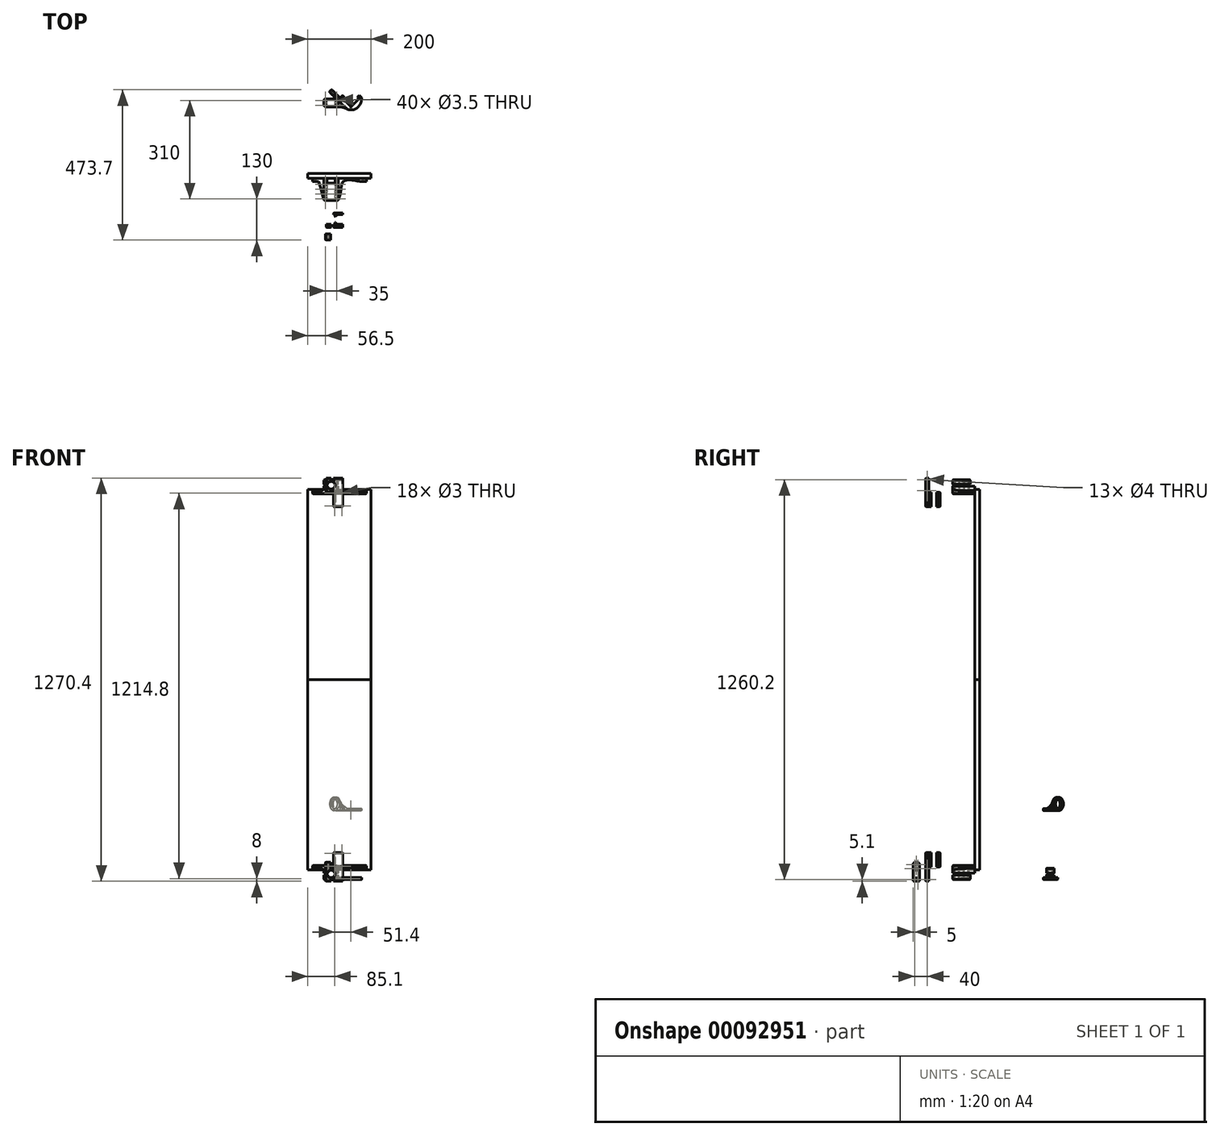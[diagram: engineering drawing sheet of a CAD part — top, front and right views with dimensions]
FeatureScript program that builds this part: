
annotation { "Feature Type Name" : "Feature", "Feature Type Description" : "" }
export const myFeature = defineFeature(function(context is Context, id is Id, definition is map)
    precondition{}
    {
        {
            var Q0;
            Q0=qCreatedBy(makeId("Top.planeOp"),FACE);
            var sketch = newSketch(context, id + "F0", { "sketchPlane" : qUnion([Q0])});
            skLineSegment(sketch, "E0", {"start": v(-59, 0) * mm, "end": v(111, 0) * mm});
            skLineSegment(sketch, "E1", {"start": v(-59, 0) * mm, "end": v(-59, -10) * mm});
            skLineSegment(sketch, "E2", {"start": v(-59, -10) * mm, "end": v(-39, -10) * mm});
            skLineSegment(sketch, "E3", {"start": v(-39, -10) * mm, "end": v(-22.5, -70) * mm});
            skLineSegment(sketch, "E4", {"start": v(-22.5, -70) * mm, "end": v(22.5, -70) * mm});
            skLineSegment(sketch, "E5", {"start": v(22.5, -70) * mm, "end": v(39, -10) * mm});
            skLineSegment(sketch, "E6", {"start": v(39, -10) * mm, "end": v(111, -10) * mm});
            skLineSegment(sketch, "E7", {"start": v(111, -10) * mm, "end": v(111, 0) * mm});
            skLineSegment(sketch, "E8", {"start": v(-49, 0) * mm, "end": v(-49, -10) * mm});
            skLineSegment(sketch, "E9", {"start": v(101, 0) * mm, "end": v(101, -10) * mm});
            skLineSegment(sketch, "E10.bottom", {"start": v(-59, 15) * mm, "end": v(141, 15) * mm, "construction": true});
            skLineSegment(sketch, "E10.top", {"start": v(-59, 0) * mm, "end": v(141, 0) * mm, "construction": true});
            skLineSegment(sketch, "E10.left", {"start": v(-59, 15) * mm, "end": v(-59, 0) * mm, "construction": true});
            skLineSegment(sketch, "E10.right", {"start": v(141, 15) * mm, "end": v(141, 0) * mm, "construction": true});
            skLineSegment(sketch, "E11", {"start": v(12.6, -70) * mm, "end": v(12.6, 0) * mm, "construction": true});
            skLineSegment(sketch, "E12", {"start": v(-12.6, -70) * mm, "end": v(-12.6, 0) * mm, "construction": true});
            skLineSegment(sketch, "E13", {"start": v(-12.6, -70) * mm, "end": v(12.6, -70) * mm});
            skPoint(sketch, "E14", {"position": v(0, -70) * mm});
            skFitSpline(sketch, "E15", {"points": [v(22.5, -70) * mm, v(91, -10) * mm], "startDerivative": vector(24.75, 90) * mm, "endDerivative": vector(156, 0) * mm});
            skLineSegment(sketch, "E16", {"start": v(0, 0) * mm, "end": v(0, -70) * mm});
            skSolve(sketch);
        }
        {
            var Q0;
            Q0=qCreatedBy(makeId("Top.planeOp"),FACE);
            cPlane(context, id + "F1", {"entities" : qUnion([Q0]), "cplaneType" : CPlaneType.OFFSET, "offset" : 3 * mm, "width" : 150 * mm, "height" : 150 * mm});
        }
        {
            var Q0;
            Q0=qCreatedBy(id+"F1.planeOp",FACE);
            var sketch = newSketch(context, id + "F2", { "sketchPlane" : qUnion([Q0])});
            skLineSegment(sketch, "E17.bottom", {"start": v(17.5, -65) * mm, "end": v(-17.5, -65) * mm, "construction": true});
            skLineSegment(sketch, "E17.top", {"start": v(17.5, -20) * mm, "end": v(-17.5, -20) * mm, "construction": true});
            skLineSegment(sketch, "E17.left", {"start": v(17.5, -65) * mm, "end": v(17.5, -20) * mm, "construction": true});
            skLineSegment(sketch, "E17.right", {"start": v(-17.5, -65) * mm, "end": v(-17.5, -20) * mm, "construction": true});
            skPoint(sketch, "E17.middle", {"position": v(0, -42.5) * mm});
            skLineSegment(sketch, "E18.bottom", {"start": v(17.5, -50) * mm, "end": v(-17.5, -50) * mm, "construction": true});
            skLineSegment(sketch, "E18.top", {"start": v(17.5, -35) * mm, "end": v(-17.5, -35) * mm, "construction": true});
            skLineSegment(sketch, "E18.left", {"start": v(17.5, -50) * mm, "end": v(17.5, -35) * mm, "construction": true});
            skLineSegment(sketch, "E18.right", {"start": v(-17.5, -50) * mm, "end": v(-17.5, -35) * mm, "construction": true});
            skCircle(sketch, "E19", {"center": v(-17.5, -20) * mm, "radius": 1.75 * mm});
            skCircle(sketch, "E20", {"center": v(-17.5, -35) * mm, "radius": 1.75 * mm});
            skCircle(sketch, "E21", {"center": v(-17.5, -50) * mm, "radius": 1.75 * mm});
            skCircle(sketch, "E22", {"center": v(-17.5, -65) * mm, "radius": 1.75 * mm});
            skCircle(sketch, "E23", {"center": v(17.5, -20) * mm, "radius": 1.75 * mm});
            skCircle(sketch, "E24", {"center": v(17.5, -35) * mm, "radius": 1.75 * mm});
            skCircle(sketch, "E25", {"center": v(17.5, -50) * mm, "radius": 1.75 * mm});
            skCircle(sketch, "E26", {"center": v(17.5, -65) * mm, "radius": 1.75 * mm});
            skSolve(sketch);
        }
        {
            var Q0;
            Q0=qCreatedBy(makeId("Front.planeOp"),FACE);
            var sketch = newSketch(context, id + "F3", { "sketchPlane" : qUnion([Q0])});
            skCircle(sketch, "E27", {"center": v(0, 0) * mm, "radius": 12.6 * mm});
            skLineSegment(sketch, "E28.bottom", {"start": v(-22.5, 3) * mm, "end": v(22.5, 3) * mm});
            skLineSegment(sketch, "E28.top", {"start": v(-22.5, 27.6) * mm, "end": v(22.5, 27.6) * mm});
            skLineSegment(sketch, "E28.left", {"start": v(-22.5, 3) * mm, "end": v(-22.5, 27.6) * mm});
            skLineSegment(sketch, "E28.right", {"start": v(22.5, 3) * mm, "end": v(22.5, 27.6) * mm});
            skPoint(sketch, "E29", {"position": v(0, 12.6) * mm});
            skPoint(sketch, "E30", {"position": v(0, 27.6) * mm});
            skLineSegment(sketch, "E31.bottom", {"start": v(-22.5, -3) * mm, "end": v(22.5, -3) * mm});
            skLineSegment(sketch, "E31.top", {"start": v(-22.5, -17.6) * mm, "end": v(22.5, -17.6) * mm});
            skLineSegment(sketch, "E31.left", {"start": v(-22.5, -3) * mm, "end": v(-22.5, -17.6) * mm});
            skLineSegment(sketch, "E31.right", {"start": v(22.5, -3) * mm, "end": v(22.5, -17.6) * mm});
            skLineSegment(sketch, "E32", {"start": v(0, 3) * mm, "end": v(0, 0) * mm, "construction": true});
            skLineSegment(sketch, "E33", {"start": v(0, 0) * mm, "end": v(0, -3) * mm, "construction": true});
            skPoint(sketch, "E34", {"position": v(0, -12.6) * mm});
            skPoint(sketch, "E35", {"position": v(0, -17.6) * mm});
            skSolve(sketch);
        }
        {
            var Q0;
            Q0=makeQuery(id+"F3.imprint","IMPRINT",FACE,{"disambiguationData":[TD([[makeQuery(id+"F3.imprint","IMPRINT",EDGE,{"derivedFrom":sQuery(id+"F3.wireOp",EDGE,"E28.top")}),-1.0]])]});
            extrude(context, id + "F4", {"entities" : qUnion([Q0]), "depth" : 70 * mm});
        }
        {
            var Q0;
            Q0=makeQuery(id+"F4.opExtrude","SWEPT_FACE",FACE,{"disambiguationData":[OSD([sQuery(id+"F3.wireOp",EDGE,"E28.top")])]});
            var sketch = newSketch(context, id + "F5", { "sketchPlane" : qUnion([Q0])});
            skLineSegment(sketch, "E36.0", {"start": v(-59, 0) * mm, "end": v(-59, -10) * mm});
            skLineSegment(sketch, "E36.1", {"start": v(-59, 0) * mm, "end": v(111, 0) * mm});
            skLineSegment(sketch, "E36.2", {"start": v(111, -10) * mm, "end": v(111, 0) * mm});
            skLineSegment(sketch, "E36.3", {"start": v(91, -10) * mm, "end": v(111, -10) * mm});
            skFitSpline(sketch, "E36.4", {"points": [v(22.5, -70) * mm, v(30.75, -40) * mm, v(39, -10) * mm, v(91, -10) * mm]});
            skLineSegment(sketch, "E36.5", {"start": v(-22.5, -70) * mm, "end": v(22.5, -70) * mm});
            skLineSegment(sketch, "E36.6", {"start": v(-39, -10) * mm, "end": v(-22.5, -70) * mm});
            skLineSegment(sketch, "E36.7", {"start": v(-59, -10) * mm, "end": v(-39, -10) * mm});
            skPoint(sketch, "E37.orphan", {"position": v(39, -10) * mm});
            skSolve(sketch);
        }
        {
            var Q0;
            Q0 = qSketchRegion(id + "F5", true);
            extrude(context, id + "F6", {"entities" : qUnion([Q0]), "operationType" : NewBodyOperationType.ADD, "oppositeDirection" : true, "depth" : 10 * mm});
        }
        {
            var Q0;
            Q0=makeQuery(id+"F4.opExtrude","CAP_FACE",FACE,{"disambiguationData":[OSD([sQuery(id+"F3.wireOp",EDGE,"E27"),sQuery(id+"F3.wireOp",EDGE,"E28.bottom"),sQuery(id+"F3.wireOp",EDGE,"E28.top"),sQuery(id+"F3.wireOp",EDGE,"E28.left"),sQuery(id+"F3.wireOp",EDGE,"E28.right")])],"isStart":false});
            var sketch = newSketch(context, id + "F7", { "sketchPlane" : qUnion([Q0])});
            skLineSegment(sketch, "E38.0", {"start": v(-22.5, -3) * mm, "end": v(-22.5, -17.6) * mm});
            skLineSegment(sketch, "E38.1", {"start": v(-22.5, -3) * mm, "end": v(-12.24, -3) * mm});
            skArc(sketch, "E38.2", {"start": v(-12.24, -3) * mm, "mid": v(0, -12.6) * mm, "end": v(12.24, -3) * mm});
            skLineSegment(sketch, "E38.3", {"start": v(22.5, -3) * mm, "end": v(22.5, -17.6) * mm});
            skLineSegment(sketch, "E38.4", {"start": v(-22.5, -17.6) * mm, "end": v(22.5, -17.6) * mm});
            skLineSegment(sketch, "E39.trimOffspring", {"start": v(12.24, -3) * mm, "end": v(22.5, -3) * mm});
            skSolve(sketch);
        }
        {
            var Q0;
            Q0 = qSketchRegion(id + "F7", true);
            extrude(context, id + "F8", {"entities" : qUnion([Q0]), "oppositeDirection" : true, "depth" : 55 * mm});
        }
        {
            var Q0;
            Q0=makeQuery(id+"F6.boolean.opBoolean","INTERSECT",EDGE,{"derivedFrom":[makeQuery(id+"F4.opExtrude","SWEPT_FACE",FACE,{"disambiguationData":[OSD([sQuery(id+"F3.wireOp",EDGE,"E28.left")])]}),makeQuery(id+"F6.opExtrude","CAP_FACE",FACE,{"disambiguationData":[OSD([sQuery(id+"F5.wireOp",EDGE,"E36.0"),sQuery(id+"F5.wireOp",EDGE,"E36.1"),sQuery(id+"F5.wireOp",EDGE,"E36.2"),sQuery(id+"F5.wireOp",EDGE,"E36.3"),sQuery(id+"F5.wireOp",EDGE,"E36.4"),sQuery(id+"F5.wireOp",EDGE,"E36.5"),sQuery(id+"F5.wireOp",EDGE,"E36.6"),sQuery(id+"F5.wireOp",EDGE,"E36.7")])],"isStart":false})]});
            var Q1;
            Q1=makeQuery(id+"F6.boolean.opBoolean","INTERSECT",EDGE,{"derivedFrom":[makeQuery(id+"F4.opExtrude","SWEPT_FACE",FACE,{"disambiguationData":[OSD([sQuery(id+"F3.wireOp",EDGE,"E28.right")])]}),makeQuery(id+"F6.opExtrude","CAP_FACE",FACE,{"disambiguationData":[OSD([sQuery(id+"F5.wireOp",EDGE,"E36.0"),sQuery(id+"F5.wireOp",EDGE,"E36.1"),sQuery(id+"F5.wireOp",EDGE,"E36.2"),sQuery(id+"F5.wireOp",EDGE,"E36.3"),sQuery(id+"F5.wireOp",EDGE,"E36.4"),sQuery(id+"F5.wireOp",EDGE,"E36.5"),sQuery(id+"F5.wireOp",EDGE,"E36.6"),sQuery(id+"F5.wireOp",EDGE,"E36.7")])],"isStart":false})]});
            fillet(context, id + "F9", {"entities" : qUnion([Q0, Q1]), "radius" : 10 * mm, "tangentPropagation" : true, "allowEdgeOverflow" : false});
        }
        {
            var Q0;
            {var subQ0=sQuery(id+"F3.wireOp",EDGE,"E28.left");Q0=makeQuery(id+"F6.boolean.opBoolean","MERGE",EDGE,{"derivedFrom":[makeQuery(id+"F4.opExtrude","CAP_EDGE",EDGE,{"disambiguationData":[OSD([subQ0])],"isStart":false}),makeQuery(id+"F6.opExtrude","SWEPT_EDGE",EDGE,{"disambiguationData":[OSD([sQuery(id+"F3.wireOp",EDGE,"E28.top"),subQ0,sQuery(id+"F5.wireOp",EDGE,"E36.5"),sQuery(id+"F5.wireOp",EDGE,"E36.6")])]})]});}
            var Q1;
            {var subQ0=sQuery(id+"F3.wireOp",EDGE,"E28.right");Q1=makeQuery(id+"F6.boolean.opBoolean","MERGE",EDGE,{"derivedFrom":[makeQuery(id+"F4.opExtrude","CAP_EDGE",EDGE,{"disambiguationData":[OSD([subQ0])],"isStart":false}),makeQuery(id+"F6.opExtrude","SWEPT_EDGE",EDGE,{"disambiguationData":[OSD([sQuery(id+"F3.wireOp",EDGE,"E28.top"),subQ0,sQuery(id+"F5.wireOp",EDGE,"E36.4"),sQuery(id+"F5.wireOp",EDGE,"E36.5")])]})]});}
            var Q2;
            Q2=makeQuery(id+"F8.opExtrude","CAP_EDGE",EDGE,{"disambiguationData":[OSD([sQuery(id+"F7.wireOp",EDGE,"E38.3")])],"isStart":true});
            var Q3;
            Q3=makeQuery(id+"F8.opExtrude","CAP_EDGE",EDGE,{"disambiguationData":[OSD([sQuery(id+"F7.wireOp",EDGE,"E38.0")])],"isStart":true});
            var Q4;
            Q4=makeQuery(id+"F8.opExtrude","CAP_EDGE",EDGE,{"disambiguationData":[OSD([sQuery(id+"F7.wireOp",EDGE,"E38.0")])],"isStart":false});
            var Q5;
            Q5=makeQuery(id+"F8.opExtrude","CAP_EDGE",EDGE,{"disambiguationData":[OSD([sQuery(id+"F7.wireOp",EDGE,"E38.3")])],"isStart":false});
            fillet(context, id + "F10", {"entities" : qUnion([Q0, Q1, Q2, Q3, Q4, Q5]), "radius" : 5 * mm, "tangentPropagation" : true, "allowEdgeOverflow" : false});
        }
        {
            var Q0;
            Q0 = qSketchRegion(id + "F2", true);
            extrude(context, id + "F11", {"entities" : qUnion([Q0]), "operationType" : NewBodyOperationType.REMOVE, "endBound" : BoundingType.SYMMETRIC, "oppositeDirection" : true, "depth" : 50 * mm});
        }
        {
            var Q0;
            Q0=makeQuery(id+"F8.opExtrude","SWEPT_EDGE",EDGE,{"disambiguationData":[OSD([sQuery(id+"F7.wireOp",EDGE,"E38.0"),sQuery(id+"F7.wireOp",EDGE,"E38.4")])]});
            var Q1;
            Q1=makeQuery(id+"F6.boolean.opBoolean","MERGE",EDGE,{"derivedFrom":[makeQuery(id+"F4.opExtrude","CAP_EDGE",EDGE,{"disambiguationData":[OSD([sQuery(id+"F3.wireOp",EDGE,"E28.top")])],"isStart":true}),makeQuery(id+"F6.opExtrude","CAP_EDGE",EDGE,{"disambiguationData":[OSD([sQuery(id+"F5.wireOp",EDGE,"E36.1")])],"isStart":true})]});
            var Q2;
            Q2=makeQuery(id+"F6.opExtrude","CAP_EDGE",EDGE,{"disambiguationData":[OSD([sQuery(id+"F5.wireOp",EDGE,"E36.6")])],"isStart":true});
            var Q3;
            Q3=makeQuery(id+"F6.opExtrude","CAP_EDGE",EDGE,{"disambiguationData":[OSD([sQuery(id+"F5.wireOp",EDGE,"E36.0")])],"isStart":true});
            var Q4;
            Q4=makeQuery(id+"F6.opExtrude","CAP_EDGE",EDGE,{"disambiguationData":[OSD([sQuery(id+"F5.wireOp",EDGE,"E36.2")])],"isStart":true});
            chamfer(context, id + "F12", {"entities" : qUnion([Q0, Q1, Q2, Q3, Q4]), "width" : 2 * mm, "tangentPropagation" : true});
        }
        {
            var Q0;
            Q0=makeQuery(id+"F6.boolean.opBoolean","MERGE",FACE,{"derivedFrom":[makeQuery(id+"F4.opExtrude","CAP_FACE",FACE,{"disambiguationData":[OSD([sQuery(id+"F3.wireOp",EDGE,"E27"),sQuery(id+"F3.wireOp",EDGE,"E28.bottom"),sQuery(id+"F3.wireOp",EDGE,"E28.top"),sQuery(id+"F3.wireOp",EDGE,"E28.left"),sQuery(id+"F3.wireOp",EDGE,"E28.right")])],"isStart":true}),makeQuery(id+"F6.opExtrude","SWEPT_FACE",FACE,{"disambiguationData":[OSD([sQuery(id+"F5.wireOp",EDGE,"E36.1")])]})]});
            var sketch = newSketch(context, id + "F13", { "sketchPlane" : qUnion([Q0])});
            skCircle(sketch, "E40", {"center": v(-101, 22.6) * mm, "radius": 2 * mm});
            skCircle(sketch, "E41", {"center": v(49, 22.6) * mm, "radius": 2 * mm});
            skSolve(sketch);
        }
        {
            var Q0;
            Q0 = qSketchRegion(id + "F13", true);
            var Q1;
            Q1=makeQuery(id+"F6.opExtrude","SWEPT_FACE",FACE,{"disambiguationData":[OSD([sQuery(id+"F5.wireOp",EDGE,"E36.3")])]});
            extrude(context, id + "F14", {"entities" : qUnion([Q0]), "operationType" : NewBodyOperationType.REMOVE, "endBound" : BoundingType.UP_TO_SURFACE, "oppositeDirection" : true, "endBoundEntityFace" : qUnion([Q1]), "depth" : 25 * mm});
        }
        {
            var Q0;
            Q0=qCreatedBy(makeId("Right.planeOp"),FACE);
            var sketch = newSketch(context, id + "F15", { "sketchPlane" : qUnion([Q0])});
            skLineSegment(sketch, "E42", {"start": v(-70, 12.6) * mm, "end": v(-69.5, 11.73) * mm});
            skLineSegment(sketch, "E43", {"start": v(-69.5, 11.73) * mm, "end": v(-69, 12.6) * mm});
            skLineSegment(sketch, "E44", {"start": v(-69, 12.6) * mm, "end": v(-70, 12.6) * mm});
            skSolve(sketch);
        }
        {
            var Q0;
            Q0 = qSketchRegion(id + "F15", true);
            var Q1;
            Q1=sQuery(id+"F0.wireOp",EDGE,"E16");
            revolve(context, id + "F16", {"operationType" : NewBodyOperationType.ADD, "entities" : qUnion([Q0]), "axis" : qUnion([Q1]), "revolveType" : RevolveType.FULL});
        }
        {
            var Q0;
            Q0=makeQuery(id+"F4.opExtrude","CAP_FACE",FACE,{"disambiguationData":[OSD([sQuery(id+"F3.wireOp",EDGE,"E27"),sQuery(id+"F3.wireOp",EDGE,"E28.bottom"),sQuery(id+"F3.wireOp",EDGE,"E28.top"),sQuery(id+"F3.wireOp",EDGE,"E28.left"),sQuery(id+"F3.wireOp",EDGE,"E28.right")])],"isStart":false});
            var sketch = newSketch(context, id + "F17", { "sketchPlane" : qUnion([Q0])});
            skLineSegment(sketch, "E45.bottom", {"start": v(-17.5, -3) * mm, "end": v(18.7, -3) * mm});
            skLineSegment(sketch, "E45.top", {"start": v(-17.5, 3) * mm, "end": v(18.7, 3) * mm});
            skLineSegment(sketch, "E45.left", {"start": v(-17.5, -3) * mm, "end": v(-17.5, 3) * mm});
            skLineSegment(sketch, "E45.right", {"start": v(18.7, -3) * mm, "end": v(18.7, 3) * mm});
            skSolve(sketch);
        }
        {
            var Q0;
            Q0 = qSketchRegion(id + "F17", true);
            extrude(context, id + "F18", {"entities" : qUnion([Q0]), "operationType" : NewBodyOperationType.REMOVE, "oppositeDirection" : true, "depth" : 25 * mm});
        }
        {
            var Q0;
            Q0=qCreatedBy(makeId("Front.planeOp"),FACE);
            var sketch = newSketch(context, id + "F19", { "sketchPlane" : qUnion([Q0])});
            skLineSegment(sketch, "E46.bottom", {"start": v(-74, 612.6) * mm, "end": v(126, 612.6) * mm});
            skLineSegment(sketch, "E46.top", {"start": v(-74, 12.6) * mm, "end": v(126, 12.6) * mm});
            skLineSegment(sketch, "E46.left", {"start": v(-74, 612.6) * mm, "end": v(-74, 12.6) * mm});
            skLineSegment(sketch, "E46.right", {"start": v(126, 612.6) * mm, "end": v(126, 12.6) * mm});
            skLineSegment(sketch, "E47.bottom", {"start": v(126, 12.6) * mm, "end": v(101, 12.6) * mm, "construction": true});
            skLineSegment(sketch, "E47.top", {"start": v(126, 22.6) * mm, "end": v(101, 22.6) * mm, "construction": true});
            skLineSegment(sketch, "E47.left", {"start": v(126, 12.6) * mm, "end": v(126, 22.6) * mm, "construction": true});
            skLineSegment(sketch, "E47.right", {"start": v(101, 12.6) * mm, "end": v(101, 22.6) * mm, "construction": true});
            skLineSegment(sketch, "E48", {"start": v(101, 22.6) * mm, "end": v(-49, 22.6) * mm, "construction": true});
            skSolve(sketch);
        }
        {
            var Q0;
            Q0=makeQuery(id+"F19.imprint","IMPRINT",FACE,{"disambiguationData":[TD([[makeQuery(id+"F19.imprint","IMPRINT",EDGE,{"derivedFrom":sQuery(id+"F19.wireOp",EDGE,"E46.bottom")}),-1.0]])]});
            extrude(context, id + "F20", {"entities" : qUnion([Q0]), "oppositeDirection" : true, "depth" : 15 * mm});
        }
        {
            var Q0;
            Q0=qCreatedBy(makeId("Front.planeOp"),FACE);
            cPlane(context, id + "F21", {"entities" : qUnion([Q0]), "cplaneType" : CPlaneType.OFFSET, "offset" : 150 * mm, "width" : 150 * mm, "height" : 150 * mm});
        }
        {
            var Q0;
            Q0=qCreatedBy(id+"F21.planeOp",FACE);
            var sketch = newSketch(context, id + "F22", { "sketchPlane" : qUnion([Q0])});
            skCircle(sketch, "E49.0", {"center": v(0, 0) * mm, "radius": 12.6 * mm});
            skLineSegment(sketch, "E50.bottom", {"start": v(8.1, -22.6) * mm, "end": v(37.1, -22.6) * mm});
            skLineSegment(sketch, "E50.top", {"start": v(8.1, 68) * mm, "end": v(37.1, 68) * mm});
            skLineSegment(sketch, "E50.left", {"start": v(8.1, -22.6) * mm, "end": v(8.1, 68) * mm});
            skLineSegment(sketch, "E50.right", {"start": v(37.1, -22.6) * mm, "end": v(37.1, 68) * mm});
            skPoint(sketch, "E51", {"position": v(12.6, 0) * mm});
            skLineSegment(sketch, "E52", {"start": v(12.6, 68) * mm, "end": v(12.6, -22.6) * mm, "construction": true});
            skLineSegment(sketch, "E53", {"start": v(32.6, 68) * mm, "end": v(32.6, -22.6) * mm, "construction": true});
            skLineSegment(sketch, "E54.bottom", {"start": v(11.1, 25) * mm, "end": v(34.1, 25) * mm, "construction": true});
            skLineSegment(sketch, "E54.top", {"start": v(11.1, 65) * mm, "end": v(34.1, 65) * mm, "construction": true});
            skLineSegment(sketch, "E54.left", {"start": v(11.1, 25) * mm, "end": v(11.1, 65) * mm, "construction": true});
            skLineSegment(sketch, "E54.right", {"start": v(34.1, 25) * mm, "end": v(34.1, 65) * mm, "construction": true});
            skCircle(sketch, "E55", {"center": v(11.1, 65) * mm, "radius": 1.5 * mm});
            skCircle(sketch, "E56", {"center": v(11.1, 25) * mm, "radius": 1.5 * mm});
            skCircle(sketch, "E57", {"center": v(34.1, 25) * mm, "radius": 1.5 * mm});
            skCircle(sketch, "E58", {"center": v(34.1, 65) * mm, "radius": 1.5 * mm});
            skPoint(sketch, "E59", {"position": v(22.6, 68) * mm});
            skPoint(sketch, "E60", {"position": v(22.6, 65) * mm});
            skLineSegment(sketch, "E61", {"start": v(12.6, 17.5) * mm, "end": v(12.6, -17.5) * mm, "construction": true});
            skLineSegment(sketch, "E62.bottom", {"start": v(-15.6, -22.6) * mm, "end": v(0, -22.6) * mm});
            skLineSegment(sketch, "E62.top", {"start": v(-15.6, 22.6) * mm, "end": v(0, 22.6) * mm});
            skLineSegment(sketch, "E62.left", {"start": v(-15.6, -22.6) * mm, "end": v(-15.6, 22.6) * mm});
            skLineSegment(sketch, "E62.right", {"start": v(0, -22.6) * mm, "end": v(0, 22.6) * mm});
            skPoint(sketch, "E63", {"position": v(-12.6, 0) * mm});
            skSolve(sketch);
        }
        {
            var Q0;
            {var subQ1=sQuery(id+"F22.wireOp",EDGE,"E50.bottom");Q0=makeQuery(id+"F22.imprint","IMPRINT",FACE,{"disambiguationData":[TD([[makeQuery(id+"F22.imprint","IMPRINT",EDGE,{"derivedFrom":subQ1}),1.0]])]});}
            var Q1;
            {var subQ4=sQuery(id+"F22.wireOp",EDGE,"E62.bottom");Q1=makeQuery(id+"F22.imprint","IMPRINT",FACE,{"disambiguationData":[TD([[makeQuery(id+"F22.imprint","IMPRINT",EDGE,{"derivedFrom":subQ4}),1.0]])]});}
            extrude(context, id + "F23", {"entities" : qUnion([Q0, Q1]), "endBound" : BoundingType.SYMMETRIC, "depth" : 10 * mm});
        }
        {
            var Q0;
            Q0=makeQuery(id+"F23.opExtrude","SWEPT_FACE",FACE,{"disambiguationData":[OSD([sQuery(id+"F22.wireOp",EDGE,"E50.top")])]});
            var sketch = newSketch(context, id + "F24", { "sketchPlane" : qUnion([Q0])});
            skLineSegment(sketch, "E64", {"start": v(8.1, -155) * mm, "end": v(8.1, -135) * mm, "construction": true});
            skPoint(sketch, "E64.endSnap0", {"position": v(8.1, -150) * mm});
            skLineSegment(sketch, "E65", {"start": v(8.1, -135) * mm, "end": v(14.1, -135) * mm, "construction": true});
            skLineSegment(sketch, "E66", {"start": v(14.1, -135) * mm, "end": v(14.1, -145) * mm, "construction": true});
            skLineSegment(sketch, "E67", {"start": v(14.1, -145) * mm, "end": v(37.1, -145) * mm, "construction": true});
            skLineSegment(sketch, "E68", {"start": v(37.1, -145) * mm, "end": v(37.1, -155) * mm});
            skLineSegment(sketch, "E69", {"start": v(37.1, -155) * mm, "end": v(8.1, -155) * mm});
            skLineSegment(sketch, "E70", {"start": v(8.1, -125) * mm, "end": v(8.1, -110) * mm, "construction": true});
            skLineSegment(sketch, "E71", {"start": v(8.1, -110) * mm, "end": v(37.1, -110) * mm});
            skLineSegment(sketch, "E72", {"start": v(37.1, -110) * mm, "end": v(37.1, -115) * mm});
            skLineSegment(sketch, "E73", {"start": v(37.1, -115) * mm, "end": v(14.1, -115) * mm, "construction": true});
            skLineSegment(sketch, "E74", {"start": v(14.1, -115) * mm, "end": v(14.1, -125) * mm, "construction": true});
            skLineSegment(sketch, "E75", {"start": v(14.1, -125) * mm, "end": v(8.1, -125) * mm, "construction": true});
            skLineSegment(sketch, "E76", {"start": v(12.6, -145) * mm, "end": v(12.6, -135) * mm});
            skArc(sketch, "E77", {"start": v(12.6, -135) * mm, "mid": v(15.53, -142.07) * mm, "end": v(22.6, -145) * mm});
            skLineSegment(sketch, "E78", {"start": v(22.6, -145) * mm, "end": v(37.1, -145) * mm});
            skLineSegment(sketch, "E79", {"start": v(8.1, -150) * mm, "end": v(8.1, -145) * mm});
            skLineSegment(sketch, "E80", {"start": v(8.1, -145) * mm, "end": v(12.6, -145) * mm});
            skArc(sketch, "E81", {"start": v(22.6, -115) * mm, "mid": v(15.53, -117.93) * mm, "end": v(12.6, -125) * mm});
            skLineSegment(sketch, "E82", {"start": v(8.1, -110) * mm, "end": v(8.1, -115) * mm});
            skLineSegment(sketch, "E83", {"start": v(8.1, -115) * mm, "end": v(12.6, -115) * mm});
            skLineSegment(sketch, "E84", {"start": v(12.6, -115) * mm, "end": v(12.6, -125) * mm});
            skLineSegment(sketch, "E85", {"start": v(22.6, -115) * mm, "end": v(37.1, -115) * mm});
            skSolve(sketch);
        }
        {
            var Q0;
            Q0=makeQuery(id+"F24.imprint","IMPRINT",FACE,{"disambiguationData":[TD([[makeQuery(id+"F24.imprint","IMPRINT",EDGE,{"derivedFrom":sQuery(id+"F24.wireOp",EDGE,"E71")}),-1.0]])]});
            var Q1;
            {var subQ0=sQuery(id+"F24.wireOp",EDGE,"E76");Q1=makeQuery(id+"F24.imprint","IMPRINT",FACE,{"disambiguationData":[TD([[makeQuery(id+"F24.imprint","IMPRINT",EDGE,{"derivedFrom":subQ0}),-1.0]])]});}
            extrude(context, id + "F25", {"entities" : qUnion([Q0, Q1]), "operationType" : NewBodyOperationType.ADD, "oppositeDirection" : true, "depth" : 46 * mm});
        }
        {
            var Q0;
            Q0=makeQuery(id+"F25.opExtrude","SWEPT_FACE",FACE,{"disambiguationData":[OSD([sQuery(id+"F24.wireOp",EDGE,"E71")])]});
            var sketch = newSketch(context, id + "F26", { "sketchPlane" : qUnion([Q0])});
            skCircle(sketch, "E86.0", {"center": v(-11.1, 25) * mm, "radius": 1.5 * mm});
            skCircle(sketch, "E86.1", {"center": v(-11.1, 65) * mm, "radius": 1.5 * mm});
            skCircle(sketch, "E86.2", {"center": v(-34.1, 25) * mm, "radius": 1.5 * mm});
            skCircle(sketch, "E86.3", {"center": v(-34.1, 65) * mm, "radius": 1.5 * mm});
            skSolve(sketch);
        }
        {
            var Q0;
            Q0 = qSketchRegion(id + "F26", true);
            extrude(context, id + "F27", {"entities" : qUnion([Q0]), "operationType" : NewBodyOperationType.REMOVE, "oppositeDirection" : true, "depth" : 25 * mm});
        }
        {
            var Q0;
            Q0=makeQuery(id+"F23.opExtrude","SWEPT_FACE",FACE,{"disambiguationData":[OSD([sQuery(id+"F22.wireOp",EDGE,"E50.right")])]});
            var sketch = newSketch(context, id + "F28", { "sketchPlane" : qUnion([Q0])});
            skPoint(sketch, "E87.0", {"position": v(-150, 17.5) * mm});
            skPoint(sketch, "E87.1", {"position": v(-150, -17.5) * mm});
            skCircle(sketch, "E88", {"center": v(-150, 17.5) * mm, "radius": 2 * mm});
            skCircle(sketch, "E89", {"center": v(-150, -17.5) * mm, "radius": 2 * mm});
            skSolve(sketch);
        }
        {
            var Q0;
            Q0 = qSketchRegion(id + "F28", true);
            extrude(context, id + "F29", {"entities" : qUnion([Q0]), "operationType" : NewBodyOperationType.REMOVE, "oppositeDirection" : true, "depth" : 55 * mm});
        }
        {
            var Q0;
            Q0=makeQuery(id+"F23.opExtrude","CAP_EDGE",EDGE,{"disambiguationData":[OSD([sQuery(id+"F22.wireOp",EDGE,"E50.right")])],"isStart":false});
            var Q1;
            Q1=makeQuery(id+"F23.opExtrude","CAP_EDGE",EDGE,{"disambiguationData":[OSD([sQuery(id+"F22.wireOp",EDGE,"E50.bottom")])],"isStart":false});
            var Q2;
            {var subQ0=sQuery(id+"F22.wireOp",EDGE,"E50.left");Q2=makeQuery(id+"F23.opExtrude","CAP_EDGE",EDGE,{"disambiguationData":[OSD([subQ0]),TDD([makeQuery(id+"F22.imprint","IMPRINT",EDGE,{"disambiguationData":[TD([[makeQuery(id+"F22.imprint","INTERSECT",VERTEX,{"derivedFrom":[sQuery(id+"F22.wireOp",EDGE,"E50.bottom"),subQ0]}),-1.0]])],"derivedFrom":subQ0})])],"isStart":false});}
            var Q3;
            {var subQ0=sQuery(id+"F22.wireOp",EDGE,"E50.left");var subQ1=sQuery(id+"F22.wireOp",EDGE,"E49.0");Q3=makeQuery(id+"F23.opExtrude","CAP_EDGE",EDGE,{"disambiguationData":[OSD([subQ1]),TDD([makeQuery(id+"F22.imprint","IMPRINT",EDGE,{"disambiguationData":[TD([[makeQuery(id+"F22.imprint","INTERSECT",VERTEX,{"disambiguationData":[OD(0.0)],"derivedFrom":[subQ1,subQ0]}),-1.0]])],"derivedFrom":subQ1})])],"isStart":false});}
            var Q4;
            {var subQ0=sQuery(id+"F22.wireOp",EDGE,"E50.left");Q4=makeQuery(id+"F23.opExtrude","CAP_EDGE",EDGE,{"disambiguationData":[OSD([subQ0]),TDD([makeQuery(id+"F22.imprint","IMPRINT",EDGE,{"disambiguationData":[TD([[makeQuery(id+"F22.imprint","INTERSECT",VERTEX,{"derivedFrom":[sQuery(id+"F22.wireOp",EDGE,"E50.top"),subQ0]}),1.0]])],"derivedFrom":subQ0})])],"isStart":false});}
            var Q5;
            Q5=makeQuery(id+"F23.opExtrude","CAP_EDGE",EDGE,{"disambiguationData":[OSD([sQuery(id+"F22.wireOp",EDGE,"E50.top")])],"isStart":false});
            var Q6;
            {var subQ0=sQuery(id+"F22.wireOp",EDGE,"E62.right");var subQ1=sQuery(id+"F22.wireOp",EDGE,"E49.0");Q6=makeQuery(id+"F23.opExtrude","CAP_EDGE",EDGE,{"disambiguationData":[OSD([subQ1]),TDD([makeQuery(id+"F22.imprint","IMPRINT",EDGE,{"disambiguationData":[TD([[makeQuery(id+"F22.imprint","INTERSECT",VERTEX,{"disambiguationData":[OD(0.0)],"derivedFrom":[subQ1,subQ0]}),1.0]])],"derivedFrom":subQ1})])],"isStart":false});}
            var Q7;
            Q7=makeQuery(id+"F23.opExtrude","CAP_EDGE",EDGE,{"disambiguationData":[OSD([sQuery(id+"F22.wireOp",EDGE,"E62.bottom")])],"isStart":false});
            var Q8;
            Q8=makeQuery(id+"F23.opExtrude","CAP_EDGE",EDGE,{"disambiguationData":[OSD([sQuery(id+"F22.wireOp",EDGE,"E62.left")])],"isStart":false});
            var Q9;
            {var subQ0=sQuery(id+"F22.wireOp",EDGE,"E62.right");Q9=makeQuery(id+"F23.opExtrude","CAP_EDGE",EDGE,{"disambiguationData":[OSD([subQ0]),TDD([makeQuery(id+"F22.imprint","IMPRINT",EDGE,{"disambiguationData":[TD([[makeQuery(id+"F22.imprint","INTERSECT",VERTEX,{"derivedFrom":[sQuery(id+"F22.wireOp",EDGE,"E62.top"),subQ0]}),1.0]])],"derivedFrom":subQ0})])],"isStart":false});}
            var Q10;
            {var subQ0=sQuery(id+"F22.wireOp",EDGE,"E62.right");Q10=makeQuery(id+"F23.opExtrude","CAP_EDGE",EDGE,{"disambiguationData":[OSD([subQ0]),TDD([makeQuery(id+"F22.imprint","IMPRINT",EDGE,{"disambiguationData":[TD([[makeQuery(id+"F22.imprint","INTERSECT",VERTEX,{"derivedFrom":[sQuery(id+"F22.wireOp",EDGE,"E62.bottom"),subQ0]}),-1.0]])],"derivedFrom":subQ0})])],"isStart":false});}
            var Q11;
            Q11=makeQuery(id+"F23.opExtrude","CAP_EDGE",EDGE,{"disambiguationData":[OSD([sQuery(id+"F22.wireOp",EDGE,"E62.top")])],"isStart":false});
            var Q12;
            Q12=makeQuery(id+"F25.opExtrude","CAP_EDGE",EDGE,{"disambiguationData":[OSD([sQuery(id+"F24.wireOp",EDGE,"E71")])],"isStart":false});
            var Q13;
            Q13=makeQuery(id+"F25.opExtrude","SWEPT_EDGE",EDGE,{"disambiguationData":[OSD([sQuery(id+"F24.wireOp",EDGE,"E71"),sQuery(id+"F24.wireOp",EDGE,"E82")])]});
            var Q14;
            Q14=makeQuery(id+"F25.opExtrude","SWEPT_EDGE",EDGE,{"disambiguationData":[OSD([sQuery(id+"F24.wireOp",EDGE,"E71"),sQuery(id+"F24.wireOp",EDGE,"E72")])]});
            var Q15;
            Q15=makeQuery(id+"F25.opExtrude","CAP_EDGE",EDGE,{"disambiguationData":[OSD([sQuery(id+"F24.wireOp",EDGE,"E71")])],"isStart":true});
            chamfer(context, id + "F30", {"entities" : qUnion([Q0, Q1, Q2, Q3, Q4, Q5, Q6, Q7, Q8, Q9, Q10, Q11, Q12, Q13, Q14, Q15]), "width" : 1 * mm, "tangentPropagation" : true});
        }
        {
            var Q0;
            Q0=makeQuery(id+"F25.opExtrude","SWEPT_EDGE",EDGE,{"disambiguationData":[OSD([sQuery(id+"F24.wireOp",EDGE,"E76"),sQuery(id+"F24.wireOp",EDGE,"E77")])]});
            var Q1;
            Q1=makeQuery(id+"F25.opExtrude","SWEPT_EDGE",EDGE,{"disambiguationData":[OSD([sQuery(id+"F24.wireOp",EDGE,"E81"),sQuery(id+"F24.wireOp",EDGE,"E84")])]});
            chamfer(context, id + "F31", {"entities" : qUnion([Q0, Q1]), "width" : 0.3 * mm, "tangentPropagation" : true});
        }
        {
            var Q0;
            Q0=makeQuery(id+"F20.opExtrude","SWEPT_BODY",BODY,{"disambiguationData":[OSD([sQuery(id+"F19.wireOp",EDGE,"E46.bottom"),sQuery(id+"F19.wireOp",EDGE,"E46.top"),sQuery(id+"F19.wireOp",EDGE,"E46.left"),sQuery(id+"F19.wireOp",EDGE,"E46.right")])]});
            var Q1;
            Q1=makeQuery(id+"F18.boolean.opBoolean","SPLIT",BODY,{"disambiguationData":[OD(0.0)],"derivedFrom":makeQuery(id+"F4.opExtrude","SWEPT_BODY",BODY,{"disambiguationData":[OSD([sQuery(id+"F3.wireOp",EDGE,"E27"),sQuery(id+"F3.wireOp",EDGE,"E28.bottom"),sQuery(id+"F3.wireOp",EDGE,"E28.top"),sQuery(id+"F3.wireOp",EDGE,"E28.left"),sQuery(id+"F3.wireOp",EDGE,"E28.right")])]})});
            var Q2;
            Q2=makeQuery(id+"F18.boolean.opBoolean","SPLIT",BODY,{"disambiguationData":[OD(1.0)],"derivedFrom":makeQuery(id+"F4.opExtrude","SWEPT_BODY",BODY,{"disambiguationData":[OSD([sQuery(id+"F3.wireOp",EDGE,"E27"),sQuery(id+"F3.wireOp",EDGE,"E28.bottom"),sQuery(id+"F3.wireOp",EDGE,"E28.top"),sQuery(id+"F3.wireOp",EDGE,"E28.left"),sQuery(id+"F3.wireOp",EDGE,"E28.right")])]})});
            var Q3;
            Q3=makeQuery(id+"F25.opExtrude","SWEPT_BODY",BODY,{"disambiguationData":[OSD([sQuery(id+"F24.wireOp",EDGE,"E71"),sQuery(id+"F24.wireOp",EDGE,"E72"),sQuery(id+"F24.wireOp",EDGE,"E81"),sQuery(id+"F24.wireOp",EDGE,"E82"),sQuery(id+"F24.wireOp",EDGE,"E83"),sQuery(id+"F24.wireOp",EDGE,"E84"),sQuery(id+"F24.wireOp",EDGE,"E85")])]});
            var Q4;
            Q4=makeQuery(id+"F23.opExtrude","SWEPT_BODY",BODY,{"disambiguationData":[OSD([sQuery(id+"F22.wireOp",EDGE,"E49.0"),sQuery(id+"F22.wireOp",EDGE,"E50.bottom"),sQuery(id+"F22.wireOp",EDGE,"E50.top"),sQuery(id+"F22.wireOp",EDGE,"E50.left"),sQuery(id+"F22.wireOp",EDGE,"E50.right"),sQuery(id+"F22.wireOp",EDGE,"E55"),sQuery(id+"F22.wireOp",EDGE,"E56"),sQuery(id+"F22.wireOp",EDGE,"E57"),sQuery(id+"F22.wireOp",EDGE,"E58")])]});
            var Q5;
            Q5=makeQuery(id+"F23.opExtrude","SWEPT_BODY",BODY,{"disambiguationData":[OSD([sQuery(id+"F22.wireOp",EDGE,"E49.0"),sQuery(id+"F22.wireOp",EDGE,"E62.bottom"),sQuery(id+"F22.wireOp",EDGE,"E62.top"),sQuery(id+"F22.wireOp",EDGE,"E62.left"),sQuery(id+"F22.wireOp",EDGE,"E62.right")])]});
            var Q6;
            Q6=makeQuery(id+"F20.opExtrude","SWEPT_FACE",FACE,{"disambiguationData":[OSD([sQuery(id+"F19.wireOp",EDGE,"E46.bottom")])]});
            mirror(context, id + "F32", {"entities" : qUnion([Q0, Q1, Q2, Q3, Q4, Q5]), "mirrorPlane" : qUnion([Q6])});
        }
        {
            var Q0;
            Q0=qCreatedBy(id+"F21.planeOp",FACE);
            cPlane(context, id + "F33", {"entities" : qUnion([Q0]), "cplaneType" : CPlaneType.OFFSET, "offset" : 400 * mm, "oppositeDirection" : true, "width" : 150 * mm, "height" : 150 * mm});
        }
        {
            var Q0;
            Q0=qCreatedBy(id+"F33.planeOp",FACE);
            var sketch = newSketch(context, id + "F34", { "sketchPlane" : qUnion([Q0])});
            skArc(sketch, "E90.0", {"start": v(12.24, 3) * mm, "mid": v(0, 12.6) * mm, "end": v(-12.24, 3) * mm});
            skLineSegment(sketch, "E90.1", {"start": v(-22.5, 3) * mm, "end": v(-12.24, 3) * mm});
            skLineSegment(sketch, "E90.2", {"start": v(-22.5, 27.6) * mm, "end": v(22.5, 27.6) * mm, "construction": true});
            skLineSegment(sketch, "E90.3", {"start": v(-22.5, 3) * mm, "end": v(-22.5, 27.6) * mm, "construction": true});
            skLineSegment(sketch, "E90.4", {"start": v(22.5, 3) * mm, "end": v(22.5, 27.6) * mm, "construction": true});
            skPoint(sketch, "E90.5", {"position": v(0, 12.6) * mm});
            skPoint(sketch, "E90.6", {"position": v(0, 27.6) * mm});
            skLineSegment(sketch, "E90.7", {"start": v(-22.5, -3) * mm, "end": v(-12.24, -3) * mm});
            skLineSegment(sketch, "E90.8", {"start": v(-22.5, -17.6) * mm, "end": v(22.5, -17.6) * mm});
            skLineSegment(sketch, "E90.9", {"start": v(-22.5, -3) * mm, "end": v(-22.5, -17.6) * mm});
            skLineSegment(sketch, "E90.10", {"start": v(22.5, -3) * mm, "end": v(22.5, -17.6) * mm});
            skPoint(sketch, "E90.13", {"position": v(0, -12.6) * mm});
            skPoint(sketch, "E90.14", {"position": v(0, -17.6) * mm});
            skLineSegment(sketch, "E91.trimOffspring", {"start": v(12.24, 3) * mm, "end": v(22.5, 3) * mm});
            skLineSegment(sketch, "E92.trimOffspring", {"start": v(12.24, -3) * mm, "end": v(22.5, -3) * mm});
            skPoint(sketch, "E90.11.end.orphan", {"position": v(0, 0) * mm});
            skPoint(sketch, "E90.11.start.orphan", {"position": v(0, 3) * mm});
            skPoint(sketch, "E90.12.start.orphan", {"position": v(0, 0) * mm});
            skArc(sketch, "E93.trimOffspring", {"start": v(-12.24, -3) * mm, "mid": v(0, -12.6) * mm, "end": v(12.24, -3) * mm});
            skPoint(sketch, "E94.orphan", {"position": v(0, -3) * mm});
            skLineSegment(sketch, "E95", {"start": v(-22.5, 18) * mm, "end": v(22.5, 18) * mm});
            skLineSegment(sketch, "E96", {"start": v(-22.5, 18) * mm, "end": v(-22.5, 3) * mm, "construction": true});
            skLineSegment(sketch, "E97", {"start": v(22.5, 18) * mm, "end": v(22.5, 3) * mm});
            skLineSegment(sketch, "E98", {"start": v(-22.5, 18) * mm, "end": v(-22.5, 3) * mm});
            skSolve(sketch);
        }
        {
            var Q0;
            Q0 = qSketchRegion(id + "F34", true);
            extrude(context, id + "F35", {"entities" : qUnion([Q0]), "depth" : 25 * mm});
        }
        {
            var Q0;
            Q0=makeQuery(id+"F35.opExtrude","SWEPT_FACE",FACE,{"disambiguationData":[OSD([sQuery(id+"F34.wireOp",EDGE,"E90.8")])]});
            var sketch = newSketch(context, id + "F36", { "sketchPlane" : qUnion([Q0])});
            skLineSegment(sketch, "E99", {"start": v(91.5, -254) * mm, "end": v(62.5, -225) * mm});
            skLineSegment(sketch, "E100", {"start": v(62.5, -225) * mm, "end": v(33.5, -254) * mm});
            skLineSegment(sketch, "E101", {"start": v(33.5, -254) * mm, "end": v(35.98, -256.47) * mm});
            skLineSegment(sketch, "E102", {"start": v(35.98, -261.47) * mm, "end": v(28.5, -254) * mm});
            skLineSegment(sketch, "E103", {"start": v(28.5, -254) * mm, "end": v(62.5, -220) * mm, "construction": true});
            skLineSegment(sketch, "E104", {"start": v(62.5, -220) * mm, "end": v(96.5, -254) * mm, "construction": true});
            skLineSegment(sketch, "E105", {"start": v(96.5, -254) * mm, "end": v(89.02, -261.47) * mm});
            skLineSegment(sketch, "E106", {"start": v(89.02, -256.47) * mm, "end": v(91.5, -254) * mm});
            skLineSegment(sketch, "E107", {"start": v(89.02, -261.47) * mm, "end": v(82.98, -255.43) * mm});
            skLineSegment(sketch, "E108", {"start": v(82.98, -255.43) * mm, "end": v(85.48, -252.93) * mm});
            skLineSegment(sketch, "E109", {"start": v(85.48, -252.93) * mm, "end": v(89.02, -256.47) * mm});
            skLineSegment(sketch, "E110", {"start": v(35.98, -261.47) * mm, "end": v(42.02, -255.43) * mm});
            skLineSegment(sketch, "E111", {"start": v(42.02, -255.43) * mm, "end": v(39.52, -252.93) * mm});
            skLineSegment(sketch, "E112", {"start": v(39.52, -252.93) * mm, "end": v(35.98, -256.47) * mm});
            skEllipticalArc(sketch, "E113", {});
            skPoint(sketch, "E114", {"position": v(62.5, -215) * mm});
            skArc(sketch, "E115", {"start": v(48.24, -218.6) * mm, "mid": v(35.76, -223.38) * mm, "end": v(22.5, -225) * mm});
            skFitSpline(sketch, "E116", {"points": [v(28.5, -254) * mm, v(22.5, -250) * mm], "startDerivative": vector(-11.97, 11.97) * mm, "endDerivative": vector(-6.05, 0) * mm});
            skLineSegment(sketch, "E117", {"start": v(22.5, -250) * mm, "end": v(22.5, -225) * mm});
            const initialGuessF36  = {"E113": [0.0625, -0.25399137802864846, -1, 0, 0.03399137802864847, 0.03899137802864845, 3.141592653589793, 5.145389248454646]};
            skSetInitialGuess(sketch, initialGuessF36);
            skSolve(sketch);
        }
        {
            var Q0;
            Q0=makeQuery(id+"F36.imprint","IMPRINT",FACE,{"disambiguationData":[TD([[makeQuery(id+"F36.imprint","IMPRINT",EDGE,{"derivedFrom":sQuery(id+"F36.wireOp",EDGE,"E99")}),-1.0]])]});
            extrude(context, id + "F37", {"entities" : qUnion([Q0]), "operationType" : NewBodyOperationType.ADD, "oppositeDirection" : true, "depth" : 6 * mm});
        }
        {
            var Q0;
            Q0=makeQuery(id+"F35.opExtrude","CAP_FACE",FACE,{"disambiguationData":[OSD([sQuery(id+"F34.wireOp",EDGE,"E90.7"),sQuery(id+"F34.wireOp",EDGE,"E90.8"),sQuery(id+"F34.wireOp",EDGE,"E90.9"),sQuery(id+"F34.wireOp",EDGE,"E90.10"),sQuery(id+"F34.wireOp",EDGE,"E92.trimOffspring"),sQuery(id+"F34.wireOp",EDGE,"E93.trimOffspring")])],"isStart":true});
            var sketch = newSketch(context, id + "F38", { "sketchPlane" : qUnion([Q0])});
            skCircle(sketch, "E118", {"center": v(-62.5, -14.6) * mm, "radius": 1.5 * mm});
            skSolve(sketch);
        }
        {
            var Q0;
            Q0 = qSketchRegion(id + "F38", true);
            extrude(context, id + "F39", {"entities" : qUnion([Q0]), "operationType" : NewBodyOperationType.REMOVE, "oppositeDirection" : true, "depth" : 40 * mm});
        }
        {
            var Q0;
            Q0=makeQuery(id+"F37.boolean.opBoolean","SPLIT",EDGE,{"derivedFrom":makeQuery(id+"F35.opExtrude","CAP_EDGE",EDGE,{"disambiguationData":[OSD([sQuery(id+"F34.wireOp",EDGE,"E90.10")])],"isStart":false})});
            var Q1;
            Q1=makeQuery(id+"F37.boolean.opBoolean","SPLIT",EDGE,{"derivedFrom":makeQuery(id+"F35.opExtrude","CAP_EDGE",EDGE,{"disambiguationData":[OSD([sQuery(id+"F34.wireOp",EDGE,"E90.10")])],"isStart":true})});
            var Q2;
            Q2=makeQuery(id+"F35.opExtrude","CAP_EDGE",EDGE,{"disambiguationData":[OSD([sQuery(id+"F34.wireOp",EDGE,"E97")])],"isStart":false});
            var Q3;
            Q3=makeQuery(id+"F35.opExtrude","CAP_EDGE",EDGE,{"disambiguationData":[OSD([sQuery(id+"F34.wireOp",EDGE,"E97")])],"isStart":true});
            var Q4;
            Q4=makeQuery(id+"F35.opExtrude","CAP_EDGE",EDGE,{"disambiguationData":[OSD([sQuery(id+"F34.wireOp",EDGE,"E98")])],"isStart":true});
            var Q5;
            Q5=makeQuery(id+"F35.opExtrude","CAP_EDGE",EDGE,{"disambiguationData":[OSD([sQuery(id+"F34.wireOp",EDGE,"E90.9")])],"isStart":true});
            var Q6;
            Q6=makeQuery(id+"F35.opExtrude","CAP_EDGE",EDGE,{"disambiguationData":[OSD([sQuery(id+"F34.wireOp",EDGE,"E98")])],"isStart":false});
            var Q7;
            Q7=makeQuery(id+"F35.opExtrude","CAP_EDGE",EDGE,{"disambiguationData":[OSD([sQuery(id+"F34.wireOp",EDGE,"E90.9")])],"isStart":false});
            fillet(context, id + "F40", {"entities" : qUnion([Q0, Q1, Q2, Q3, Q4, Q5, Q6, Q7]), "radius" : 5 * mm, "tangentPropagation" : true, "allowEdgeOverflow" : false});
        }
        {
            var Q0;
            Q0=qCreatedBy(makeId("Right.planeOp"),FACE);
            var sketch = newSketch(context, id + "F41", { "sketchPlane" : qUnion([Q0])});
            skLineSegment(sketch, "E119", {"start": v(225, -12.6) * mm, "end": v(225, -11.6) * mm});
            skLineSegment(sketch, "E120", {"start": v(225, -11.6) * mm, "end": v(226, -12.6) * mm});
            skLineSegment(sketch, "E121", {"start": v(226, -12.6) * mm, "end": v(225, -12.6) * mm});
            skPoint(sketch, "E122", {"position": v(225, -12.6) * mm});
            skLineSegment(sketch, "E123", {"start": v(224.37, 0) * mm, "end": v(238.8, 0) * mm});
            skSolve(sketch);
        }
        {
            var Q0;
            Q0 = qSketchRegion(id + "F41", true);
            var Q1;
            Q1=sQuery(id+"F41.wireOp",EDGE,"E123");
            revolve(context, id + "F42", {"operationType" : NewBodyOperationType.ADD, "entities" : qUnion([Q0]), "axis" : qUnion([Q1]), "revolveType" : RevolveType.FULL});
        }
        {
            var Q0;
            Q0=makeQuery(id+"F42.boolean.opBoolean","MERGE",FACE,{"derivedFrom":[makeQuery(id+"F35.opExtrude","CAP_FACE",FACE,{"disambiguationData":[OSD([sQuery(id+"F34.wireOp",EDGE,"E90.0"),sQuery(id+"F34.wireOp",EDGE,"E90.1"),sQuery(id+"F34.wireOp",EDGE,"E91.trimOffspring"),sQuery(id+"F34.wireOp",EDGE,"E95"),sQuery(id+"F34.wireOp",EDGE,"E97"),sQuery(id+"F34.wireOp",EDGE,"E98")])],"isStart":false}),makeQuery(id+"F35.opExtrude","CAP_FACE",FACE,{"disambiguationData":[OSD([sQuery(id+"F34.wireOp",EDGE,"E90.7"),sQuery(id+"F34.wireOp",EDGE,"E90.8"),sQuery(id+"F34.wireOp",EDGE,"E90.9"),sQuery(id+"F34.wireOp",EDGE,"E90.10"),sQuery(id+"F34.wireOp",EDGE,"E92.trimOffspring"),sQuery(id+"F34.wireOp",EDGE,"E93.trimOffspring")])],"isStart":false}),makeQuery(id+"F42.opRevolve","SWEPT_FACE",FACE,{"disambiguationData":[OSD([sQuery(id+"F41.wireOp",EDGE,"E119")])]})]});
            var sketch = newSketch(context, id + "F43", { "sketchPlane" : qUnion([Q0])});
            skLineSegment(sketch, "E124.bottom", {"start": v(-17.5, -3) * mm, "end": v(17.5, -3) * mm});
            skLineSegment(sketch, "E124.top", {"start": v(-17.5, 3) * mm, "end": v(17.5, 3) * mm});
            skLineSegment(sketch, "E124.left", {"start": v(-17.5, -3) * mm, "end": v(-17.5, 3) * mm});
            skLineSegment(sketch, "E124.right", {"start": v(17.5, -3) * mm, "end": v(17.5, 3) * mm});
            skSolve(sketch);
        }
        {
            var Q0;
            Q0 = qSketchRegion(id + "F43", true);
            extrude(context, id + "F44", {"entities" : qUnion([Q0]), "operationType" : NewBodyOperationType.REMOVE, "oppositeDirection" : true, "depth" : 25 * mm});
        }
        {
            var Q0;
            Q0=makeQuery(id+"F35.opExtrude","SWEPT_FACE",FACE,{"disambiguationData":[OSD([sQuery(id+"F34.wireOp",EDGE,"E95")])]});
            var sketch = newSketch(context, id + "F45", { "sketchPlane" : qUnion([Q0])});
            skLineSegment(sketch, "E125.bottom", {"start": v(-17.5, 245) * mm, "end": v(17.5, 245) * mm, "construction": true});
            skLineSegment(sketch, "E125.top", {"start": v(-17.5, 230) * mm, "end": v(17.5, 230) * mm, "construction": true});
            skLineSegment(sketch, "E125.left", {"start": v(-17.5, 245) * mm, "end": v(-17.5, 230) * mm, "construction": true});
            skLineSegment(sketch, "E125.right", {"start": v(17.5, 245) * mm, "end": v(17.5, 230) * mm, "construction": true});
            skCircle(sketch, "E126", {"center": v(-17.5, 245) * mm, "radius": 1.75 * mm});
            skCircle(sketch, "E127", {"center": v(-17.5, 230) * mm, "radius": 1.75 * mm});
            skCircle(sketch, "E128", {"center": v(17.5, 230) * mm, "radius": 1.75 * mm});
            skCircle(sketch, "E129", {"center": v(17.5, 245) * mm, "radius": 1.75 * mm});
            skSolve(sketch);
        }
        {
            var Q0;
            Q0 = qSketchRegion(id + "F45", true);
            extrude(context, id + "F46", {"entities" : qUnion([Q0]), "operationType" : NewBodyOperationType.REMOVE, "oppositeDirection" : true, "depth" : 50 * mm});
        }
        {
            var Q0;
            Q0=makeQuery(id+"F37.boolean.opBoolean","MERGE",FACE,{"derivedFrom":[makeQuery(id+"F35.opExtrude","SWEPT_FACE",FACE,{"disambiguationData":[OSD([sQuery(id+"F34.wireOp",EDGE,"E90.8")])]}),makeQuery(id+"F37.opExtrude","CAP_FACE",FACE,{"disambiguationData":[OSD([sQuery(id+"F36.wireOp",EDGE,"E99"),sQuery(id+"F36.wireOp",EDGE,"E100"),sQuery(id+"F36.wireOp",EDGE,"E101"),sQuery(id+"F36.wireOp",EDGE,"E102"),sQuery(id+"F36.wireOp",EDGE,"E105"),sQuery(id+"F36.wireOp",EDGE,"E106"),sQuery(id+"F36.wireOp",EDGE,"E107"),sQuery(id+"F36.wireOp",EDGE,"E108"),sQuery(id+"F36.wireOp",EDGE,"E109"),sQuery(id+"F36.wireOp",EDGE,"E110"),sQuery(id+"F36.wireOp",EDGE,"E111"),sQuery(id+"F36.wireOp",EDGE,"E112"),sQuery(id+"F36.wireOp",EDGE,"E113"),sQuery(id+"F36.wireOp",EDGE,"E115"),sQuery(id+"F36.wireOp",EDGE,"E116"),sQuery(id+"F36.wireOp",EDGE,"E117")])],"isStart":true})]});
            var Q1;
            Q1=makeQuery(id+"F35.opExtrude","SWEPT_FACE",FACE,{"disambiguationData":[OSD([sQuery(id+"F34.wireOp",EDGE,"E95")])]});
            chamfer(context, id + "F47", {"entities" : qUnion([Q0, Q1]), "width" : 1 * mm, "tangentPropagation" : true});
        }
        {
            var Q0;
            Q0=qCreatedBy(makeId("Top.planeOp"),FACE);
            cPlane(context, id + "F48", {"entities" : qUnion([Q0]), "cplaneType" : CPlaneType.OFFSET, "offset" : 200 * mm, "width" : 150 * mm, "height" : 150 * mm});
        }
        {
            var Q0;
            Q0=qCreatedBy(id+"F48.planeOp",FACE);
            var sketch = newSketch(context, id + "F49", { "sketchPlane" : qUnion([Q0])});
            skLineSegment(sketch, "E130.0", {"start": v(62.5, 225) * mm, "end": v(33.5, 254) * mm});
            skLineSegment(sketch, "E130.1", {"start": v(33.5, 254) * mm, "end": v(35.98, 256.47) * mm});
            skLineSegment(sketch, "E130.2", {"start": v(39.52, 252.93) * mm, "end": v(35.98, 256.47) * mm});
            skLineSegment(sketch, "E130.3", {"start": v(42.02, 255.43) * mm, "end": v(39.52, 252.93) * mm});
            skLineSegment(sketch, "E130.4", {"start": v(35.98, 261.47) * mm, "end": v(42.02, 255.43) * mm});
            skLineSegment(sketch, "E130.5", {"start": v(35.98, 261.47) * mm, "end": v(28.5, 254) * mm});
            skLineSegment(sketch, "E130.6", {"start": v(85.48, 252.93) * mm, "end": v(89.02, 256.47) * mm});
            skLineSegment(sketch, "E130.7", {"start": v(89.02, 256.47) * mm, "end": v(91.5, 254) * mm});
            skLineSegment(sketch, "E130.8", {"start": v(91.5, 254) * mm, "end": v(62.5, 225) * mm});
            skLineSegment(sketch, "E130.9", {"start": v(82.98, 255.43) * mm, "end": v(85.48, 252.93) * mm});
            skLineSegment(sketch, "E130.10", {"start": v(89.02, 261.47) * mm, "end": v(82.98, 255.43) * mm});
            skLineSegment(sketch, "E130.11", {"start": v(96.5, 254) * mm, "end": v(89.02, 261.47) * mm});
            skEllipticalArc(sketch, "E130.12", {});
            skLineSegment(sketch, "E131", {"start": v(48.24, 218.6) * mm, "end": v(20.68, 246.16) * mm});
            skLineSegment(sketch, "E132", {"start": v(20.68, 246.16) * mm, "end": v(28.5, 254) * mm});
            const initialGuessF49  = {"E130.12": [0.0625, 0.25399137802864846, 0, 1, 0.03899137802864845, 0.03399137802864847, 2.708592385519837, 4.71238898038469]};
            skSetInitialGuess(sketch, initialGuessF49);
            skSolve(sketch);
        }
        {
            var Q0;
            Q0 = qSketchRegion(id + "F49", true);
            extrude(context, id + "F50", {"entities" : qUnion([Q0]), "depth" : 6 * mm});
        }
        {
            var Q0;
            Q0=qCreatedBy(id+"F33.planeOp",FACE);
            var sketch = newSketch(context, id + "F51", { "sketchPlane" : qUnion([Q0])});
            skCircle(sketch, "E133", {"center": v(62.5, 203) * mm, "radius": 1.5 * mm});
            skSolve(sketch);
        }
        {
            var Q0;
            Q0 = qSketchRegion(id + "F51", true);
            extrude(context, id + "F52", {"entities" : qUnion([Q0]), "operationType" : NewBodyOperationType.REMOVE, "depth" : 40 * mm});
        }
        {
            var Q0;
            Q0=makeQuery(id+"F50.opExtrude","SWEPT_FACE",FACE,{"disambiguationData":[OSD([sQuery(id+"F49.wireOp",EDGE,"E131")])]});
            var sketch = newSketch(context, id + "F53", { "sketchPlane" : qUnion([Q0])});
            skCircle(sketch, "E134", {"center": v(-175.46, 221) * mm, "radius": 15 * mm});
            skArc(sketch, "E135", {"start": v(-156.22, 229.4) * mm, "mid": v(-193.03, 232.5) * mm, "end": v(-175.46, 200) * mm});
            skPoint(sketch, "E136", {"position": v(-175.46, 200) * mm});
            skLineSegment(sketch, "E137", {"start": v(-175.46, 200) * mm, "end": v(-120.46, 200) * mm});
            skLineSegment(sketch, "E138", {"start": v(-120.46, 200) * mm, "end": v(-120.46, 206) * mm});
            skArc(sketch, "E139", {"start": v(-120.46, 206) * mm, "mid": v(-141.83, 212.37) * mm, "end": v(-156.22, 229.4) * mm});
            skSolve(sketch);
        }
        {
            var Q0;
            Q0 = qSketchRegion(id + "F53", true);
            extrude(context, id + "F54", {"entities" : qUnion([Q0]), "operationType" : NewBodyOperationType.ADD, "oppositeDirection" : true, "depth" : 10 * mm});
        }
        {
            var Q0;
            Q0=makeQuery(id+"F54.boolean.opBoolean","INTERSECT",EDGE,{"derivedFrom":[makeQuery(id+"F50.opExtrude","CAP_FACE",FACE,{"disambiguationData":[OSD([sQuery(id+"F49.wireOp",EDGE,"E130.0"),sQuery(id+"F49.wireOp",EDGE,"E130.1"),sQuery(id+"F49.wireOp",EDGE,"E130.2"),sQuery(id+"F49.wireOp",EDGE,"E130.3"),sQuery(id+"F49.wireOp",EDGE,"E130.4"),sQuery(id+"F49.wireOp",EDGE,"E130.5"),sQuery(id+"F49.wireOp",EDGE,"E130.6"),sQuery(id+"F49.wireOp",EDGE,"E130.7"),sQuery(id+"F49.wireOp",EDGE,"E130.8"),sQuery(id+"F49.wireOp",EDGE,"E130.9"),sQuery(id+"F49.wireOp",EDGE,"E130.10"),sQuery(id+"F49.wireOp",EDGE,"E130.11"),sQuery(id+"F49.wireOp",EDGE,"E130.12"),sQuery(id+"F49.wireOp",EDGE,"E131"),sQuery(id+"F49.wireOp",EDGE,"E132")])],"isStart":false}),makeQuery(id+"F54.opExtrude","CAP_FACE",FACE,{"disambiguationData":[OSD([sQuery(id+"F53.wireOp",EDGE,"E134"),sQuery(id+"F53.wireOp",EDGE,"E135"),sQuery(id+"F53.wireOp",EDGE,"E137"),sQuery(id+"F53.wireOp",EDGE,"E138"),sQuery(id+"F53.wireOp",EDGE,"E139")])],"isStart":false})]});
            fillet(context, id + "F55", {"entities" : qUnion([Q0]), "radius" : 20 * mm, "tangentPropagation" : true, "allowEdgeOverflow" : false});
        }
        {
            var Q0;
            Q0=makeQuery(id+"F54.boolean.opBoolean","MERGE",FACE,{"derivedFrom":[makeQuery(id+"F50.opExtrude","CAP_FACE",FACE,{"disambiguationData":[OSD([sQuery(id+"F49.wireOp",EDGE,"E130.0"),sQuery(id+"F49.wireOp",EDGE,"E130.1"),sQuery(id+"F49.wireOp",EDGE,"E130.2"),sQuery(id+"F49.wireOp",EDGE,"E130.3"),sQuery(id+"F49.wireOp",EDGE,"E130.4"),sQuery(id+"F49.wireOp",EDGE,"E130.5"),sQuery(id+"F49.wireOp",EDGE,"E130.6"),sQuery(id+"F49.wireOp",EDGE,"E130.7"),sQuery(id+"F49.wireOp",EDGE,"E130.8"),sQuery(id+"F49.wireOp",EDGE,"E130.9"),sQuery(id+"F49.wireOp",EDGE,"E130.10"),sQuery(id+"F49.wireOp",EDGE,"E130.11"),sQuery(id+"F49.wireOp",EDGE,"E130.12"),sQuery(id+"F49.wireOp",EDGE,"E131"),sQuery(id+"F49.wireOp",EDGE,"E132")])],"isStart":true}),makeQuery(id+"F54.opExtrude","SWEPT_FACE",FACE,{"disambiguationData":[OSD([sQuery(id+"F53.wireOp",EDGE,"E137")])]})]});
            chamfer(context, id + "F56", {"entities" : qUnion([Q0]), "width" : 1 * mm, "tangentPropagation" : true});
        }
        {
            var Q0;
            Q0=qCreatedBy(id+"F21.planeOp",FACE);
            cPlane(context, id + "F57", {"entities" : qUnion([Q0]), "cplaneType" : CPlaneType.OFFSET, "offset" : 25 * mm, "width" : 150 * mm, "height" : 150 * mm});
        }
        {
            var Q0;
            Q0=qCreatedBy(id+"F57.planeOp",FACE);
            var sketch = newSketch(context, id + "F58", { "sketchPlane" : qUnion([Q0])});
            skLineSegment(sketch, "E140.0", {"start": v(-15.6, 22.6) * mm, "end": v(-2, 22.6) * mm});
            skArc(sketch, "E140.1", {"start": v(-2, 12.44) * mm, "mid": v(-12.6, 0) * mm, "end": v(-2, -12.44) * mm});
            skLineSegment(sketch, "E140.2", {"start": v(-15.6, -22.6) * mm, "end": v(-2, -22.6) * mm});
            skLineSegment(sketch, "E141", {"start": v(-2, 12.44) * mm, "end": v(-2, 22.6) * mm});
            skLineSegment(sketch, "E142", {"start": v(-2, -12.44) * mm, "end": v(-2, -22.6) * mm});
            skPoint(sketch, "E143.orphan", {"position": v(0, 22.6) * mm});
            skPoint(sketch, "E144.orphan", {"position": v(0, -22.6) * mm});
            skLineSegment(sketch, "E145.bottom", {"start": v(-15.6, 22.6) * mm, "end": v(-17.6, 22.6) * mm});
            skLineSegment(sketch, "E145.top", {"start": v(-15.6, -22.6) * mm, "end": v(-17.6, -22.6) * mm});
            skLineSegment(sketch, "E145.right", {"start": v(-17.6, 22.6) * mm, "end": v(-17.6, -22.6) * mm});
            skSolve(sketch);
        }
        {
            var Q0;
            Q0 = qSketchRegion(id + "F58", true);
            extrude(context, id + "F59", {"entities" : qUnion([Q0]), "depth" : 20 * mm});
        }
        {
            var Q0;
            Q0=makeQuery(id+"F59.opExtrude","SWEPT_FACE",FACE,{"disambiguationData":[OSD([sQuery(id+"F58.wireOp",EDGE,"E145.right")])]});
            var sketch = newSketch(context, id + "F60", { "sketchPlane" : qUnion([Q0])});
            skLineSegment(sketch, "E146.bottom", {"start": v(180, 17.5) * mm, "end": v(190, 17.5) * mm, "construction": true});
            skLineSegment(sketch, "E146.top", {"start": v(180, -17.5) * mm, "end": v(190, -17.5) * mm, "construction": true});
            skLineSegment(sketch, "E146.left", {"start": v(180, 17.5) * mm, "end": v(180, -17.5) * mm, "construction": true});
            skLineSegment(sketch, "E146.right", {"start": v(190, 17.5) * mm, "end": v(190, -17.5) * mm, "construction": true});
            skCircle(sketch, "E147", {"center": v(180, 17.5) * mm, "radius": 2 * mm});
            skCircle(sketch, "E148", {"center": v(190, 17.5) * mm, "radius": 2 * mm});
            skCircle(sketch, "E149", {"center": v(180, -17.5) * mm, "radius": 2 * mm});
            skCircle(sketch, "E150", {"center": v(190, -17.5) * mm, "radius": 2 * mm});
            skSolve(sketch);
        }
        {
            var Q0;
            Q0 = qSketchRegion(id + "F60", true);
            extrude(context, id + "F61", {"entities" : qUnion([Q0]), "operationType" : NewBodyOperationType.REMOVE, "oppositeDirection" : true, "depth" : 25 * mm});
        }
        {
            var Q0;
            Q0=makeQuery(id+"F59.opExtrude","SWEPT_FACE",FACE,{"disambiguationData":[OSD([sQuery(id+"F58.wireOp",EDGE,"E140.0"),sQuery(id+"F58.wireOp",EDGE,"E145.bottom")])]});
            extrude(context, id + "F62", {"entities" : qUnion([Q0]), "operationType" : NewBodyOperationType.ADD, "depth" : 15 * mm, "offsetDistance" : 25 * mm});
        }
        {
            var Q0;
            {var subQ0=sQuery(id+"F58.wireOp",EDGE,"E145.bottom");var subQ1=sQuery(id+"F58.wireOp",EDGE,"E140.0");Q0=makeQuery(id+"F62.opExtrude","CAP_EDGE",EDGE,{"disambiguationData":[OSD([subQ1,subQ0]),TDD([makeQuery(id+"F59.opExtrude","CAP_EDGE",EDGE,{"disambiguationData":[OSD([subQ1,subQ0])],"isStart":true})])],"isStart":false});}
            var Q1;
            {var subQ0=sQuery(id+"F58.wireOp",EDGE,"E145.bottom");var subQ1=sQuery(id+"F58.wireOp",EDGE,"E140.0");Q1=makeQuery(id+"F62.opExtrude","CAP_EDGE",EDGE,{"disambiguationData":[OSD([subQ1,subQ0]),TDD([makeQuery(id+"F59.opExtrude","CAP_EDGE",EDGE,{"disambiguationData":[OSD([subQ1,subQ0])],"isStart":false})])],"isStart":false});}
            fillet(context, id + "F63", {"entities" : qUnion([Q0, Q1]), "radius" : 7.5 * mm, "tangentPropagation" : true, "allowEdgeOverflow" : false});
        }
        {
            var Q0;
            {var subQ0=sQuery(id+"F58.wireOp",EDGE,"E145.right");Q0=makeQuery(id+"F62.boolean.opBoolean","MERGE",FACE,{"derivedFrom":[makeQuery(id+"F59.opExtrude","SWEPT_FACE",FACE,{"disambiguationData":[OSD([subQ0])]}),makeQuery(id+"F62.opExtrude","SWEPT_FACE",FACE,{"disambiguationData":[OSD([sQuery(id+"F58.wireOp",EDGE,"E145.bottom"),subQ0])]})]});}
            var sketch = newSketch(context, id + "F64", { "sketchPlane" : qUnion([Q0])});
            skCircle(sketch, "E151", {"center": v(185, 30.1) * mm, "radius": 2 * mm});
            skSolve(sketch);
        }
        {
            var Q0;
            Q0 = qSketchRegion(id + "F64", true);
            extrude(context, id + "F65", {"entities" : qUnion([Q0]), "operationType" : NewBodyOperationType.REMOVE, "oppositeDirection" : true, "depth" : 25 * mm, "offsetDistance" : 25 * mm});
        }
        {
            var Q0;
            {var subQ0=sQuery(id+"F58.wireOp",EDGE,"E145.right");Q0=makeQuery(id+"F62.boolean.opBoolean","MERGE",FACE,{"derivedFrom":[makeQuery(id+"F59.opExtrude","SWEPT_FACE",FACE,{"disambiguationData":[OSD([subQ0])]}),makeQuery(id+"F62.opExtrude","SWEPT_FACE",FACE,{"disambiguationData":[OSD([sQuery(id+"F58.wireOp",EDGE,"E145.bottom"),subQ0])]})]});}
            chamfer(context, id + "F66", {"entities" : qUnion([Q0]), "width" : 1 * mm, "tangentPropagation" : true});
        }
    });
